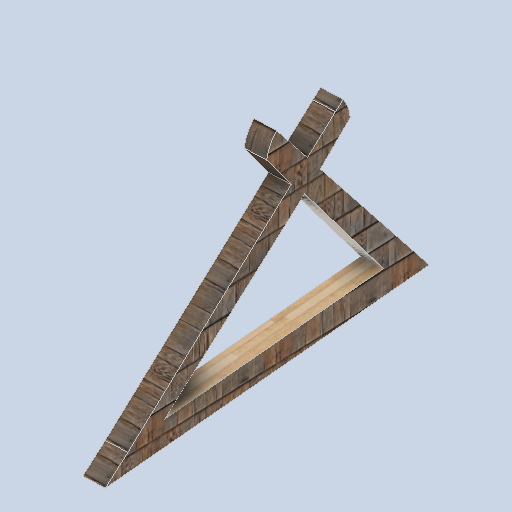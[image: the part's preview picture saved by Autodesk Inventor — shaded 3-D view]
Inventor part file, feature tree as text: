
AUTODESK INVENTOR PART (.ipt)
format: ipt  version: 2024.2 (Build 282272000, 272)  size: 223,744 bytes
history: native  units: in
note: dims shown in document units (in); Inventor stores cm internally (conversion verified against a paired STEP export)
features: sketch x9, plane x6, other x3
ambient origin geometry x8: Origin, YZ Plane, XZ Plane, XY Plane, X Axis, Y Axis, Z Axis, Center Point
bodies: Solid1 (feature_tree)
feature tree (18):
  other  "pad_outframe_03_MIR.ipt"
  other  "Solid1::pad_outframe_03_MIR.ipt"
  other  "TaggingFeature1"
  sketch  "Sketch1"  dims[d0=0.3937in]
  sketch  "Sketch2"
  sketch  "Sketch3"
  sketch  "Sketch6"
  sketch  "Sketch7"
  sketch  "Sketch8"
  sketch  "Sketch9"
  sketch  "Sketch10"
  sketch  "Sketch11"
  plane  "Work Plane1"
  plane  "Work Plane2"
  plane  "Work Plane3"
  plane  "Work Plane4"
  plane  "Work Plane5"
  plane  "Work Plane6"
